# Revit family: Roxtec knock-out sleeve KOS
name_source: partatom
category: Duct Accessories
revit_build: Autodesk Revit 2017 (Build: 20190508_0315(x64)
units: mm (PartAtom-declared; Revit-internal decimal feet)

## family parameters
Cut with Voids When Loaded = No
Host = Face
Part Type = Attaches To
Round Connector Dimension = Use Diameter
Shared = No

## types (6) — shared parameters
Description = Sealing solutions for cables and pipes
ETIM Classification = EC001174
Knock-out plate offset = 85 mm  [stored 0.278871 ft]
Manufacturer = Roxtec
Material = ABS Plastic
URL = https://www.roxtec.com
Version = 2.0
zero-valued in all types: Default Elevation, NominalDepth, NominalHeight

## per-type parameters (varying)
| type | D | Diameter A | L | Sähkönumero | W | Weight (kg) |
| KOS 100/110 D=150 | 150 mm | 102 mm | 80 mm  [stored 0.262467 ft] | 1753094 | 180 mm  [stored 0.590551 ft] | 0.4 |
| KOS 150/160 D=150 | 150 mm | 152 mm  [stored 0.498688 ft] | 80 mm  [stored 0.262467 ft] | 1753095 | 230 mm  [stored 0.754593 ft] | 0.6 |
| KOS 200/200 D=150 | 150 mm | 202 mm  [stored 0.66273 ft] | 80 mm  [stored 0.262467 ft] | 1753096 | 280 mm  [stored 0.918635 ft] | 0.8 |
| KOS 100/100 D=100 | 100 mm  [stored 0.328084 ft] | 102 mm | 48 mm  [stored 0.15748 ft] | 1753094 | 180 mm  [stored 0.590551 ft] | 0.3 |
| KOS 150/150 D=100 | 100 mm  [stored 0.328084 ft] | 152 mm  [stored 0.498688 ft] | 48 mm  [stored 0.15748 ft] | 1753095 | 230 mm  [stored 0.754593 ft] | 0.4 |
| KOS 200/200 D=100 | 100 mm  [stored 0.328084 ft] | 202 mm  [stored 0.66273 ft] | 48 mm  [stored 0.15748 ft] | 1753096 | 280 mm  [stored 0.918635 ft] | 0.6 |

note: [stored X ft] marks values corroborated as IEEE doubles in the binary element streams (Revit-internal decimal feet)

## geometry (parser evidence)
native form markers: Sweep x2
no freeform markers — native parametric forms only
